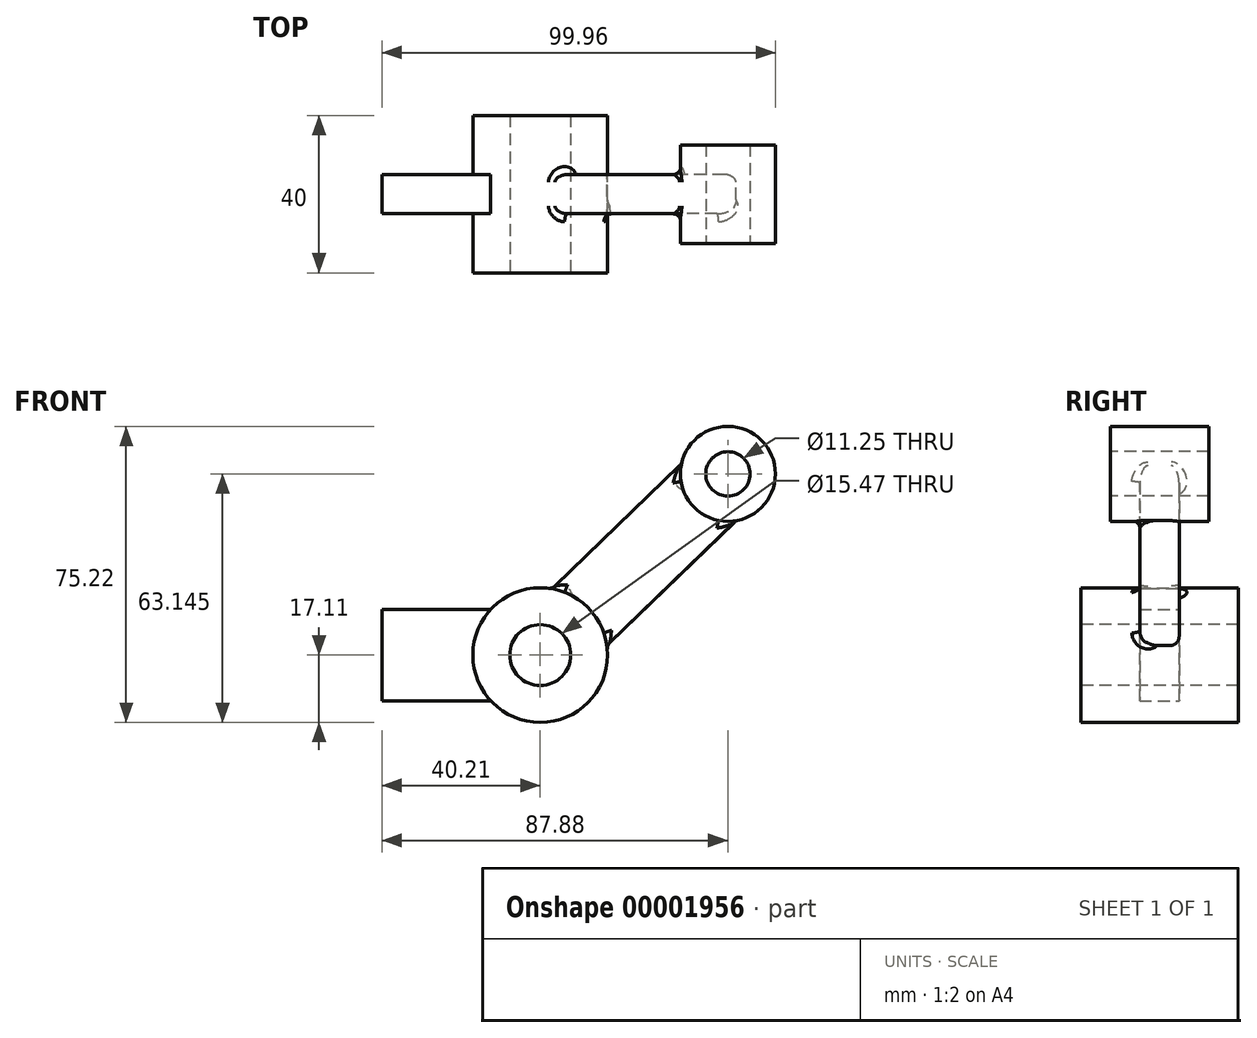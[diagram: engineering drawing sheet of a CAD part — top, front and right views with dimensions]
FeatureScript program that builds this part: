
annotation { "Feature Type Name" : "Feature", "Feature Type Description" : "" }
export const myFeature = defineFeature(function(context is Context, id is Id, definition is map)
    precondition{}
    {
        {
            var Q0;
            Q0=qCreatedBy(makeId("Front.planeOp"),FACE);
            var sketch = newSketch(context, id + "F0", { "sketchPlane" : qUnion([Q0])});
            skCircle(sketch, "E0", {"center": v(0, 0) * mm, "radius": 17.1 * mm});
            skCircle(sketch, "E1", {"center": v(0, 0) * mm, "radius": 7.74 * mm});
            skCircle(sketch, "E2", {"center": v(47.67, 46.03) * mm, "radius": 12.08 * mm});
            skCircle(sketch, "E3", {"center": v(47.67, 46.03) * mm, "radius": 5.63 * mm});
            skLineSegment(sketch, "E4", {"start": v(0, 0) * mm, "end": v(47.67, 46.03) * mm});
            skPoint(sketch, "E5", {"position": v(23.84, 23.02) * mm});
            skLineSegment(sketch, "E6.bottom", {"start": v(-40.21, -11.6) * mm, "end": v(-9.16, -11.6) * mm});
            skLineSegment(sketch, "E6.top", {"start": v(-40.21, 11.6) * mm, "end": v(-9.16, 11.6) * mm});
            skLineSegment(sketch, "E6.left", {"start": v(-40.21, -11.6) * mm, "end": v(-40.21, 11.6) * mm});
            skLineSegment(sketch, "E6.right", {"start": v(-9.16, -11.6) * mm, "end": v(-9.16, 11.6) * mm});
            skPoint(sketch, "E7", {"position": v(-9.16, 0) * mm});
            skLineSegment(sketch, "E8", {"start": v(0, 0) * mm, "end": v(64.62, 0) * mm, "construction": true});
            skSolve(sketch);
        }
        {
            var Q0;
            {var subQ6=sQuery(id+"F0.wireOp",EDGE,"E1");Q0=makeQuery(id+"F0.imprint","IMPRINT",FACE,{"disambiguationData":[TD([[makeQuery(id+"F0.imprint","IMPRINT",EDGE,{"derivedFrom":subQ6}),-1.0]])]});}
            var Q1;
            {var subQ0=sQuery(id+"F0.wireOp",EDGE,"E6.right");Q1=makeQuery(id+"F0.imprint","IMPRINT",FACE,{"disambiguationData":[TD([[makeQuery(id+"F0.imprint","IMPRINT",EDGE,{"derivedFrom":subQ0}),1.0]])]});}
            var Q2;
            {var subQ1=sQuery(id+"F0.wireOp",EDGE,"E1");Q2=makeQuery(id+"F0.imprint","IMPRINT",FACE,{"disambiguationData":[TD([[makeQuery(id+"F0.imprint","IMPRINT",EDGE,{"derivedFrom":subQ1}),1.0]])]});}
            extrude(context, id + "F1", {"entities" : qUnion([Q0, Q1, Q2]), "endBound" : BoundingType.SYMMETRIC, "depth" : 40 * mm});
        }
        {
            var Q0;
            {var subQ0=sQuery(id+"F0.wireOp",EDGE,"E6.left");Q0=makeQuery(id+"F0.imprint","IMPRINT",FACE,{"disambiguationData":[TD([[makeQuery(id+"F0.imprint","IMPRINT",EDGE,{"derivedFrom":subQ0}),-1.0]])]});}
            extrude(context, id + "F2", {"entities" : qUnion([Q0]), "operationType" : NewBodyOperationType.ADD, "endBound" : BoundingType.SYMMETRIC, "depth" : 10 * mm});
        }
        {
            var Q0;
            Q0=sQuery(id+"F0.wireOp",EDGE,"E4");
            var Q1;
            Q1=sQuery(id+"F0.wireOp",VERTEX,"E5");
            cPlane(context, id + "F3", {"entities" : qUnion([Q0, Q1]), "cplaneType" : CPlaneType.CURVE_POINT, "offset" : 150 * mm, "width" : 150 * mm, "height" : 150 * mm});
        }
        {
            var Q0;
            Q0=qCreatedBy(id+"F3.planeOp",FACE);
            var sketch = newSketch(context, id + "F4", { "sketchPlane" : qUnion([Q0])});
            skLineSegment(sketch, "E9.rect.bottom", {"start": v(5, 10) * mm, "end": v(-5, 10) * mm});
            skLineSegment(sketch, "E9.rect.top", {"start": v(5, -10) * mm, "end": v(-5, -10) * mm});
            skLineSegment(sketch, "E9.rect.left", {"start": v(5, 10) * mm, "end": v(5, -10) * mm});
            skLineSegment(sketch, "E9.rect.right", {"start": v(-5, 10) * mm, "end": v(-5, -10) * mm});
            skPoint(sketch, "E9.rect.middle", {"position": v(0, 0) * mm});
            skLineSegment(sketch, "E10", {"start": v(0, 10) * mm, "end": v(0, 30) * mm, "construction": true});
            skSolve(sketch);
        }
        {
            var Q0;
            {var subQ2=sQuery(id+"F0.wireOp",EDGE,"E2");Q0=makeQuery(id+"F0.imprint","IMPRINT",FACE,{"disambiguationData":[TD([[makeQuery(id+"F0.imprint","IMPRINT",EDGE,{"derivedFrom":subQ2}),1.0]])]});}
            var Q1;
            {var subQ1=sQuery(id+"F0.wireOp",EDGE,"E3");Q1=makeQuery(id+"F0.imprint","IMPRINT",FACE,{"disambiguationData":[TD([[makeQuery(id+"F0.imprint","IMPRINT",EDGE,{"derivedFrom":subQ1}),1.0]])]});}
            extrude(context, id + "F5", {"entities" : qUnion([Q0, Q1]), "operationType" : NewBodyOperationType.ADD, "endBound" : BoundingType.SYMMETRIC, "depth" : 25 * mm});
        }
        {
            var Q0;
            Q0=makeQuery(id+"F4.imprint","IMPRINT",FACE,{"disambiguationData":[TD([[makeQuery(id+"F4.imprint","IMPRINT",EDGE,{"derivedFrom":sQuery(id+"F4.wireOp",EDGE,"E9.rect.bottom")}),1.0]])]});
            extrude(context, id + "F6", {"entities" : qUnion([Q0]), "operationType" : NewBodyOperationType.ADD, "endBound" : BoundingType.SYMMETRIC, "depth" : 60 * mm});
        }
        {
            var Q0;
            {var subQ1=sQuery(id+"F0.wireOp",EDGE,"E1");Q0=makeQuery(id+"F0.imprint","IMPRINT",FACE,{"disambiguationData":[TD([[makeQuery(id+"F0.imprint","IMPRINT",EDGE,{"derivedFrom":subQ1}),1.0]])]});}
            var Q1;
            {var subQ1=sQuery(id+"F0.wireOp",EDGE,"E3");Q1=makeQuery(id+"F0.imprint","IMPRINT",FACE,{"disambiguationData":[TD([[makeQuery(id+"F0.imprint","IMPRINT",EDGE,{"derivedFrom":subQ1}),1.0]])]});}
            extrude(context, id + "F7", {"entities" : qUnion([Q0, Q1]), "operationType" : NewBodyOperationType.REMOVE, "endBound" : BoundingType.SYMMETRIC, "oppositeDirection" : true, "depth" : 60 * mm});
        }
        {
            var Q0;
            Q0=makeQuery(id+"F6.opExtrude","SWEPT_EDGE",EDGE,{"disambiguationData":[OSD([sQuery(id+"F4.wireOp",EDGE,"E9.rect.bottom"),sQuery(id+"F4.wireOp",EDGE,"E9.rect.left")])]});
            var Q1;
            Q1=makeQuery(id+"F6.boolean.opBoolean","INTERSECT",EDGE,{"derivedFrom":[makeQuery(id+"F5.opExtrude","SWEPT_FACE",FACE,{"disambiguationData":[OSD([sQuery(id+"F0.wireOp",EDGE,"E2")])]}),makeQuery(id+"F6.opExtrude","SWEPT_FACE",FACE,{"disambiguationData":[OSD([sQuery(id+"F4.wireOp",EDGE,"E9.rect.bottom")])]})]});
            var Q2;
            Q2=makeQuery(id+"F6.opExtrude","SWEPT_EDGE",EDGE,{"disambiguationData":[OSD([sQuery(id+"F4.wireOp",EDGE,"E9.rect.bottom"),sQuery(id+"F4.wireOp",EDGE,"E9.rect.right")])]});
            var Q3;
            Q3=makeQuery(id+"F6.boolean.opBoolean","INTERSECT",EDGE,{"derivedFrom":[makeQuery(id+"F1.opExtrude","SWEPT_FACE",FACE,{"disambiguationData":[OSD([sQuery(id+"F0.wireOp",EDGE,"E0")])]}),makeQuery(id+"F6.opExtrude","SWEPT_FACE",FACE,{"disambiguationData":[OSD([sQuery(id+"F4.wireOp",EDGE,"E9.rect.bottom")])]})]});
            var Q4;
            Q4=makeQuery(id+"F6.boolean.opBoolean","INTERSECT",EDGE,{"derivedFrom":[makeQuery(id+"F1.opExtrude","SWEPT_FACE",FACE,{"disambiguationData":[OSD([sQuery(id+"F0.wireOp",EDGE,"E0")])]}),makeQuery(id+"F6.opExtrude","SWEPT_FACE",FACE,{"disambiguationData":[OSD([sQuery(id+"F4.wireOp",EDGE,"E9.rect.right")])]})]});
            var Q5;
            Q5=makeQuery(id+"F6.opExtrude","SWEPT_EDGE",EDGE,{"disambiguationData":[OSD([sQuery(id+"F4.wireOp",EDGE,"E9.rect.top"),sQuery(id+"F4.wireOp",EDGE,"E9.rect.right")])]});
            var Q6;
            Q6=makeQuery(id+"F6.boolean.opBoolean","INTERSECT",EDGE,{"derivedFrom":[makeQuery(id+"F5.opExtrude","SWEPT_FACE",FACE,{"disambiguationData":[OSD([sQuery(id+"F0.wireOp",EDGE,"E2")])]}),makeQuery(id+"F6.opExtrude","SWEPT_FACE",FACE,{"disambiguationData":[OSD([sQuery(id+"F4.wireOp",EDGE,"E9.rect.right")])]})]});
            var Q7;
            Q7=makeQuery(id+"F6.opExtrude","SWEPT_EDGE",EDGE,{"disambiguationData":[OSD([sQuery(id+"F4.wireOp",EDGE,"E9.rect.top"),sQuery(id+"F4.wireOp",EDGE,"E9.rect.left")])]});
            fillet(context, id + "F8", {"entities" : qUnion([Q0, Q1, Q2, Q3, Q4, Q5, Q6, Q7]), "radius" : 2 * mm, "tangentPropagation" : true, "allowEdgeOverflow" : false});
        }
        {
            var Q0;
            Q0=makeQuery(id+"F1.opExtrude","SWEPT_BODY",BODY,{"disambiguationData":[OSD([sQuery(id+"F0.wireOp",EDGE,"E0")])]});
            var Q1;
            Q1=makeQuery(id+"F2.opExtrude","CAP_VERTEX",VERTEX,{"disambiguationData":[OSD([sQuery(id+"F0.wireOp",EDGE,"E6.bottom"),sQuery(id+"F0.wireOp",EDGE,"E6.left")])],"isStart":false});
            transform(context, id + "F9", {"entities" : qUnion([Q0]), "transformType" : TransformType.SCALE_UNIFORMLY, "scale" : 1, "makeCopy" : false, "scalePoint" : qUnion([Q1])});
        }
    });
